# Revit family: Komfort Roto EC SE 601(-E)
name_source: partatom
category: Mechanical Equipment
units: mm (PartAtom-declared; Revit-internal decimal feet)

## family parameters
Always vertical = Yes
Cut with Voids When Loaded = No
OmniClass Number = 23.75.00.00
OmniClass Title = Climate Control (HVAC)
Part Type = Normal
Room Calculation Point = No
Round Connector Dimension = Use Diameter
Shared = No
Work Plane-Based = No

## types (4) — shared parameters
00_20_Manufacturer = Blauberg
00_20_Name = Single-room air handling unit with heat recovery
Casing Material = Polymer-coated steel (white)
Connected air duct diameter = 200 mm  [stored 0.656168 ft]
Filter = G4
Frequency = 60 Hz
H = 749 mm
H1 = 822 mm  [stored 2.69685 ft]
L = 609 mm  [stored 1.99803 ft]
L1 = 248 mm
Load Classification = HVAC
Maintenance zone material = <By Category>
Maximum Air Flow = 747.0 m³/h
Number of Fase = 1
Sound pressure level at 3 m distance = 29 dBA
Voltage = 230 V
W = 900 mm  [stored 2.95276 ft]
Weight = 0.00 kg
zero-valued in all types: Default Elevation

## per-type parameters (varying)
| type | Amperage | Power |
| KOMFORT Roto EC S 601 | 2 A | 336 W |
| KOMFORT Roto EC S 601-E | 2 A | 336 W |
| KOMFORT Roto EC SE 601 | 9 A | 1736 W |
| KOMFORT Roto EC SE 601-E | 9 A | 1736 W |

note: column(s) folded — value = type name in every type: 00_20_Type

note: [stored X ft] marks values corroborated as IEEE doubles in the binary element streams (Revit-internal decimal feet)

## geometry (parser evidence)
native form markers: Sweep x8
no freeform markers — native parametric forms only
